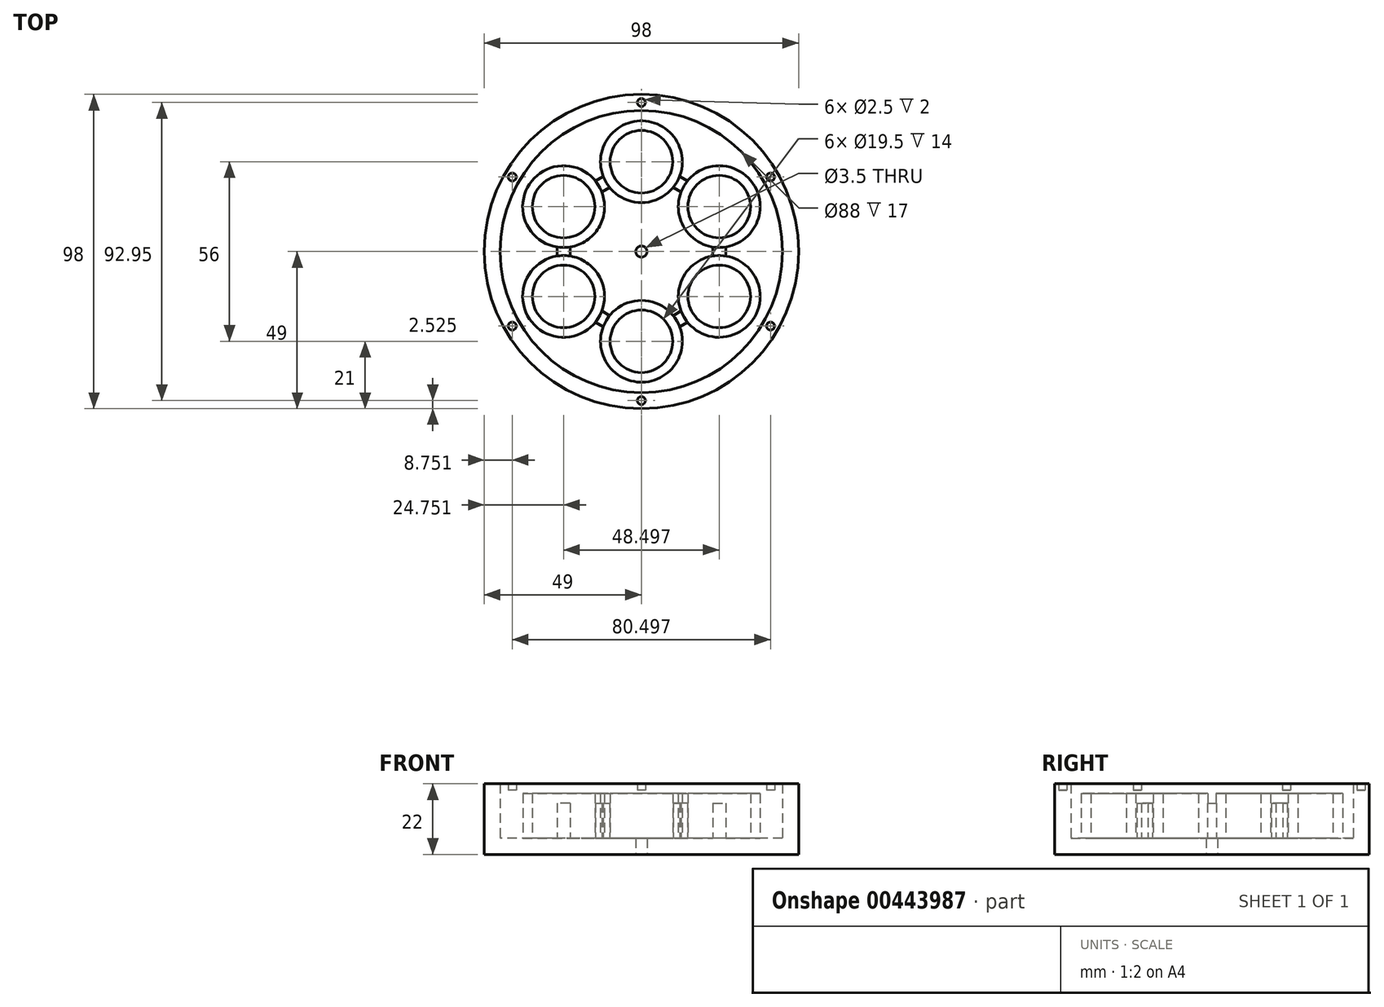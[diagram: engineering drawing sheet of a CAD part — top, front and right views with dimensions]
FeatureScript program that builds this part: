
annotation { "Feature Type Name" : "Feature", "Feature Type Description" : "" }
export const myFeature = defineFeature(function(context is Context, id is Id, definition is map)
    precondition{}
    {
        {
            var Q0;
            Q0=qCreatedBy(makeId("Top.planeOp"),FACE);
            var sketch = newSketch(context, id + "F0", { "sketchPlane" : qUnion([Q0])});
            skCircle(sketch, "E0", {"center": v(0, 0) * mm, "radius": 44 * mm});
            skLineSegment(sketch, "E1", {"start": v(0, -28) * mm, "end": v(-24.25, -14) * mm, "construction": true});
            skLineSegment(sketch, "E2", {"start": v(-24.25, -14) * mm, "end": v(-24.25, 14) * mm, "construction": true});
            skLineSegment(sketch, "E3", {"start": v(-24.25, 14) * mm, "end": v(0, 28) * mm, "construction": true});
            skLineSegment(sketch, "E4", {"start": v(0, 28) * mm, "end": v(24.25, 14) * mm, "construction": true});
            skLineSegment(sketch, "E5", {"start": v(24.25, 14) * mm, "end": v(24.25, -14) * mm, "construction": true});
            skLineSegment(sketch, "E6", {"start": v(24.25, -14) * mm, "end": v(0, -28) * mm, "construction": true});
            skLineSegment(sketch, "E7", {"start": v(24.25, 0) * mm, "end": v(17.35, 0) * mm, "construction": true});
            skPoint(sketch, "E7.endSnap0", {"position": v(24.25, 0) * mm});
            skCircle(sketch, "E8", {"center": v(0, 28) * mm, "radius": 9.75 * mm});
            skCircle(sketch, "E9", {"center": v(-24.25, 14) * mm, "radius": 9.75 * mm});
            skCircle(sketch, "E10", {"center": v(24.25, 14) * mm, "radius": 9.75 * mm});
            skCircle(sketch, "E11", {"center": v(24.25, -14) * mm, "radius": 9.75 * mm});
            skCircle(sketch, "E12", {"center": v(0, -28) * mm, "radius": 9.75 * mm});
            skCircle(sketch, "E13", {"center": v(-24.25, -14) * mm, "radius": 9.75 * mm});
            skCircle(sketch, "E14", {"center": v(0, 0) * mm, "radius": 1.75 * mm});
            skLineSegment(sketch, "E15", {"start": v(-24.25, 0) * mm, "end": v(-21.1, 0) * mm, "construction": true});
            skPoint(sketch, "E15.endSnap0", {"position": v(-24.25, 0) * mm});
            skCircle(sketch, "E16.0", {"center": v(-24.25, 14) * mm, "radius": 12.75 * mm});
            skCircle(sketch, "E17", {"center": v(-24.25, -14) * mm, "radius": 12.75 * mm});
            skCircle(sketch, "E18", {"center": v(0, -28) * mm, "radius": 12.75 * mm});
            skCircle(sketch, "E19", {"center": v(24.25, -14) * mm, "radius": 12.75 * mm});
            skCircle(sketch, "E20", {"center": v(24.25, 14) * mm, "radius": 12.75 * mm});
            skCircle(sketch, "E21", {"center": v(0, 28) * mm, "radius": 12.75 * mm});
            skCircle(sketch, "E22.0", {"center": v(0, 0) * mm, "radius": 49 * mm});
            skLineSegment(sketch, "E23.0", {"start": v(-22.25, -12.85) * mm, "end": v(-22.25, 12.85) * mm});
            skLineSegment(sketch, "E23.1", {"start": v(0, 25.7) * mm, "end": v(22.25, 12.85) * mm});
            skLineSegment(sketch, "E23.2", {"start": v(22.25, 12.85) * mm, "end": v(22.25, -12.85) * mm});
            skLineSegment(sketch, "E23.3", {"start": v(-22.25, 12.85) * mm, "end": v(0, 25.7) * mm});
            skLineSegment(sketch, "E23.4", {"start": v(22.25, -12.85) * mm, "end": v(0, -25.7) * mm});
            skLineSegment(sketch, "E23.5", {"start": v(0, -25.7) * mm, "end": v(-22.25, -12.85) * mm});
            skLineSegment(sketch, "E24.0", {"start": v(-26.25, -15.15) * mm, "end": v(-26.25, 15.15) * mm});
            skLineSegment(sketch, "E24.1", {"start": v(0, 30.3) * mm, "end": v(26.25, 15.15) * mm});
            skLineSegment(sketch, "E24.2", {"start": v(26.25, 15.15) * mm, "end": v(26.25, -15.15) * mm});
            skLineSegment(sketch, "E24.3", {"start": v(-26.25, 15.15) * mm, "end": v(0, 30.3) * mm});
            skLineSegment(sketch, "E24.4", {"start": v(26.25, -15.15) * mm, "end": v(0, -30.3) * mm});
            skLineSegment(sketch, "E24.5", {"start": v(0, -30.3) * mm, "end": v(-26.25, -15.15) * mm});
            skLineSegment(sketch, "E25.0", {"start": v(-40.25, -23.24) * mm, "end": v(-40.25, 23.24) * mm, "construction": true});
            skLineSegment(sketch, "E25.1", {"start": v(0, 46.48) * mm, "end": v(40.25, 23.24) * mm, "construction": true});
            skLineSegment(sketch, "E25.2", {"start": v(40.25, 23.24) * mm, "end": v(40.25, -23.24) * mm, "construction": true});
            skLineSegment(sketch, "E25.3", {"start": v(-40.25, 23.24) * mm, "end": v(0, 46.48) * mm, "construction": true});
            skLineSegment(sketch, "E25.4", {"start": v(40.25, -23.24) * mm, "end": v(0, -46.48) * mm, "construction": true});
            skLineSegment(sketch, "E25.5", {"start": v(0, -46.48) * mm, "end": v(-40.25, -23.24) * mm, "construction": true});
            skCircle(sketch, "E26", {"center": v(-40.25, 23.24) * mm, "radius": 1.25 * mm});
            skCircle(sketch, "E27", {"center": v(0, 46.48) * mm, "radius": 1.25 * mm});
            skCircle(sketch, "E28", {"center": v(40.25, 23.24) * mm, "radius": 1.25 * mm});
            skCircle(sketch, "E29", {"center": v(-40.25, -23.24) * mm, "radius": 1.25 * mm});
            skCircle(sketch, "E30", {"center": v(0, -46.48) * mm, "radius": 1.25 * mm});
            skCircle(sketch, "E31", {"center": v(40.25, -23.24) * mm, "radius": 1.25 * mm});
            skSolve(sketch);
        }
        {
            var Q0;
            {var subQ0=sQuery(id+"F0.wireOp",EDGE,"E24.5");var subQ1=sQuery(id+"F0.wireOp",EDGE,"E17");var subQ2=makeQuery(id+"F0.imprint","INTERSECT",VERTEX,{"derivedFrom":[subQ1,subQ0]});Q0=makeQuery(id+"F0.imprint","IMPRINT",FACE,{"disambiguationData":[TD([[makeQuery(id+"F0.imprint","IMPRINT",EDGE,{"disambiguationData":[TD([[subQ2,-1.0]])],"derivedFrom":subQ1}),-1.0]])]});}
            var Q1;
            {var subQ0=sQuery(id+"F0.wireOp",EDGE,"E23.5");var subQ1=sQuery(id+"F0.wireOp",EDGE,"E12");var subQ2=makeQuery(id+"F0.imprint","INTERSECT",VERTEX,{"derivedFrom":[subQ1,subQ0]});Q1=makeQuery(id+"F0.imprint","IMPRINT",FACE,{"disambiguationData":[TD([[makeQuery(id+"F0.imprint","IMPRINT",EDGE,{"disambiguationData":[TD([[subQ2,-1.0]])],"derivedFrom":subQ1}),-1.0]])]});}
            var Q2;
            {var subQ0=sQuery(id+"F0.wireOp",EDGE,"E24.1");var subQ1=sQuery(id+"F0.wireOp",EDGE,"E10");var subQ2=makeQuery(id+"F0.imprint","INTERSECT",VERTEX,{"derivedFrom":[subQ1,subQ0]});Q2=makeQuery(id+"F0.imprint","IMPRINT",FACE,{"disambiguationData":[TD([[makeQuery(id+"F0.imprint","IMPRINT",EDGE,{"disambiguationData":[TD([[subQ2,1.0]])],"derivedFrom":subQ1}),1.0]])]});}
            var Q3;
            Q3=makeQuery(id+"F0.imprint","IMPRINT",FACE,{"disambiguationData":[TD([[makeQuery(id+"F0.imprint","IMPRINT",EDGE,{"derivedFrom":sQuery(id+"F0.wireOp",EDGE,"E14")}),-1.0]])]});
            var Q4;
            {var subQ0=sQuery(id+"F0.wireOp",EDGE,"E24.2");var subQ1=sQuery(id+"F0.wireOp",EDGE,"E11");var subQ2=makeQuery(id+"F0.imprint","INTERSECT",VERTEX,{"derivedFrom":[subQ1,subQ0]});Q4=makeQuery(id+"F0.imprint","IMPRINT",FACE,{"disambiguationData":[TD([[makeQuery(id+"F0.imprint","IMPRINT",EDGE,{"disambiguationData":[TD([[subQ2,1.0]])],"derivedFrom":subQ1}),-1.0]])]});}
            var Q5;
            {var subQ0=sQuery(id+"F0.wireOp",EDGE,"E24.5");var subQ1=sQuery(id+"F0.wireOp",EDGE,"E13");var subQ2=makeQuery(id+"F0.imprint","INTERSECT",VERTEX,{"derivedFrom":[subQ1,subQ0]});Q5=makeQuery(id+"F0.imprint","IMPRINT",FACE,{"disambiguationData":[TD([[makeQuery(id+"F0.imprint","IMPRINT",EDGE,{"disambiguationData":[TD([[subQ2,-1.0]])],"derivedFrom":subQ1}),-1.0]])]});}
            var Q6;
            {var subQ0=sQuery(id+"F0.wireOp",EDGE,"E24.3");var subQ1=sQuery(id+"F0.wireOp",EDGE,"E8");var subQ2=makeQuery(id+"F0.imprint","INTERSECT",VERTEX,{"derivedFrom":[subQ1,subQ0]});Q6=makeQuery(id+"F0.imprint","IMPRINT",FACE,{"disambiguationData":[TD([[makeQuery(id+"F0.imprint","IMPRINT",EDGE,{"disambiguationData":[TD([[subQ2,1.0]])],"derivedFrom":subQ1}),-1.0]])]});}
            var Q7;
            {var subQ0=sQuery(id+"F0.wireOp",EDGE,"E24.3");var subQ1=sQuery(id+"F0.wireOp",EDGE,"E9");var subQ2=makeQuery(id+"F0.imprint","INTERSECT",VERTEX,{"derivedFrom":[subQ1,subQ0]});Q7=makeQuery(id+"F0.imprint","IMPRINT",FACE,{"disambiguationData":[TD([[makeQuery(id+"F0.imprint","IMPRINT",EDGE,{"disambiguationData":[TD([[subQ2,1.0]])],"derivedFrom":subQ1}),-1.0]])]});}
            var Q8;
            {var subQ0=sQuery(id+"F0.wireOp",EDGE,"E24.0");var subQ1=sQuery(id+"F0.wireOp",EDGE,"E9");var subQ2=makeQuery(id+"F0.imprint","INTERSECT",VERTEX,{"derivedFrom":[subQ1,subQ0]});Q8=makeQuery(id+"F0.imprint","IMPRINT",FACE,{"disambiguationData":[TD([[makeQuery(id+"F0.imprint","IMPRINT",EDGE,{"disambiguationData":[TD([[subQ2,-1.0]])],"derivedFrom":subQ1}),-1.0]])]});}
            var Q9;
            {var subQ0=sQuery(id+"F0.wireOp",EDGE,"E23.1");var subQ1=sQuery(id+"F0.wireOp",EDGE,"E8");var subQ2=makeQuery(id+"F0.imprint","INTERSECT",VERTEX,{"derivedFrom":[subQ1,subQ0]});Q9=makeQuery(id+"F0.imprint","IMPRINT",FACE,{"disambiguationData":[TD([[makeQuery(id+"F0.imprint","IMPRINT",EDGE,{"disambiguationData":[TD([[subQ2,-1.0]])],"derivedFrom":subQ1}),-1.0]])]});}
            var Q10;
            {var subQ0=sQuery(id+"F0.wireOp",EDGE,"E23.2");var subQ1=sQuery(id+"F0.wireOp",EDGE,"E11");var subQ2=makeQuery(id+"F0.imprint","INTERSECT",VERTEX,{"derivedFrom":[subQ1,subQ0]});Q10=makeQuery(id+"F0.imprint","IMPRINT",FACE,{"disambiguationData":[TD([[makeQuery(id+"F0.imprint","IMPRINT",EDGE,{"disambiguationData":[TD([[subQ2,-1.0]])],"derivedFrom":subQ1}),-1.0]])]});}
            var Q11;
            {var subQ0=sQuery(id+"F0.wireOp",EDGE,"E23.4");var subQ1=sQuery(id+"F0.wireOp",EDGE,"E12");var subQ2=makeQuery(id+"F0.imprint","INTERSECT",VERTEX,{"derivedFrom":[subQ1,subQ0]});Q11=makeQuery(id+"F0.imprint","IMPRINT",FACE,{"disambiguationData":[TD([[makeQuery(id+"F0.imprint","IMPRINT",EDGE,{"disambiguationData":[TD([[subQ2,1.0]])],"derivedFrom":subQ1}),-1.0]])]});}
            var Q12;
            {var subQ0=sQuery(id+"F0.wireOp",EDGE,"E23.0");var subQ1=sQuery(id+"F0.wireOp",EDGE,"E13");var subQ2=makeQuery(id+"F0.imprint","INTERSECT",VERTEX,{"derivedFrom":[subQ1,subQ0]});Q12=makeQuery(id+"F0.imprint","IMPRINT",FACE,{"disambiguationData":[TD([[makeQuery(id+"F0.imprint","IMPRINT",EDGE,{"disambiguationData":[TD([[subQ2,1.0]])],"derivedFrom":subQ1}),1.0]])]});}
            var Q13;
            {var subQ0=sQuery(id+"F0.wireOp",EDGE,"E24.4");var subQ1=sQuery(id+"F0.wireOp",EDGE,"E12");var subQ2=makeQuery(id+"F0.imprint","INTERSECT",VERTEX,{"derivedFrom":[subQ1,subQ0]});Q13=makeQuery(id+"F0.imprint","IMPRINT",FACE,{"disambiguationData":[TD([[makeQuery(id+"F0.imprint","IMPRINT",EDGE,{"disambiguationData":[TD([[subQ2,1.0]])],"derivedFrom":subQ1}),1.0]])]});}
            var Q14;
            {var subQ0=sQuery(id+"F0.wireOp",EDGE,"E23.1");var subQ1=sQuery(id+"F0.wireOp",EDGE,"E20");var subQ2=makeQuery(id+"F0.imprint","INTERSECT",VERTEX,{"derivedFrom":[subQ1,subQ0]});Q14=makeQuery(id+"F0.imprint","IMPRINT",FACE,{"disambiguationData":[TD([[makeQuery(id+"F0.imprint","IMPRINT",EDGE,{"disambiguationData":[TD([[subQ2,1.0]])],"derivedFrom":subQ1}),-1.0]])]});}
            var Q15;
            {var subQ0=sQuery(id+"F0.wireOp",EDGE,"E23.2");var subQ1=sQuery(id+"F0.wireOp",EDGE,"E10");var subQ2=makeQuery(id+"F0.imprint","INTERSECT",VERTEX,{"derivedFrom":[subQ1,subQ0]});Q15=makeQuery(id+"F0.imprint","IMPRINT",FACE,{"disambiguationData":[TD([[makeQuery(id+"F0.imprint","IMPRINT",EDGE,{"disambiguationData":[TD([[subQ2,-1.0]])],"derivedFrom":subQ1}),-1.0]])]});}
            var Q16;
            {var subQ0=sQuery(id+"F0.wireOp",EDGE,"E23.3");var subQ1=sQuery(id+"F0.wireOp",EDGE,"E8");var subQ2=makeQuery(id+"F0.imprint","INTERSECT",VERTEX,{"derivedFrom":[subQ1,subQ0]});Q16=makeQuery(id+"F0.imprint","IMPRINT",FACE,{"disambiguationData":[TD([[makeQuery(id+"F0.imprint","IMPRINT",EDGE,{"disambiguationData":[TD([[subQ2,1.0]])],"derivedFrom":subQ1}),-1.0]])]});}
            var Q17;
            {var subQ0=sQuery(id+"F0.wireOp",EDGE,"E24.4");var subQ1=sQuery(id+"F0.wireOp",EDGE,"E12");var subQ2=makeQuery(id+"F0.imprint","INTERSECT",VERTEX,{"derivedFrom":[subQ1,subQ0]});Q17=makeQuery(id+"F0.imprint","IMPRINT",FACE,{"disambiguationData":[TD([[makeQuery(id+"F0.imprint","IMPRINT",EDGE,{"disambiguationData":[TD([[subQ2,1.0]])],"derivedFrom":subQ1}),-1.0]])]});}
            var Q18;
            {var subQ0=sQuery(id+"F0.wireOp",EDGE,"E23.4");var subQ1=sQuery(id+"F0.wireOp",EDGE,"E12");var subQ2=makeQuery(id+"F0.imprint","INTERSECT",VERTEX,{"derivedFrom":[subQ1,subQ0]});Q18=makeQuery(id+"F0.imprint","IMPRINT",FACE,{"disambiguationData":[TD([[makeQuery(id+"F0.imprint","IMPRINT",EDGE,{"disambiguationData":[TD([[subQ2,-1.0]])],"derivedFrom":subQ1}),1.0]])]});}
            var Q19;
            {var subQ3=sQuery(id+"F0.wireOp",EDGE,"E13");var subQ8=sQuery(id+"F0.wireOp",EDGE,"E24.0");var subQ9=makeQuery(id+"F0.imprint","INTERSECT",VERTEX,{"derivedFrom":[subQ3,subQ8]});Q19=makeQuery(id+"F0.imprint","IMPRINT",FACE,{"disambiguationData":[TD([[makeQuery(id+"F0.imprint","IMPRINT",EDGE,{"disambiguationData":[TD([[subQ9,1.0]])],"derivedFrom":subQ3}),1.0]])]});}
            var Q20;
            {var subQ0=sQuery(id+"F0.wireOp",EDGE,"E24.2");var subQ1=sQuery(id+"F0.wireOp",EDGE,"E11");var subQ2=makeQuery(id+"F0.imprint","INTERSECT",VERTEX,{"derivedFrom":[subQ1,subQ0]});Q20=makeQuery(id+"F0.imprint","IMPRINT",FACE,{"disambiguationData":[TD([[makeQuery(id+"F0.imprint","IMPRINT",EDGE,{"disambiguationData":[TD([[subQ2,1.0]])],"derivedFrom":subQ1}),1.0]])]});}
            var Q21;
            {var subQ0=sQuery(id+"F0.wireOp",EDGE,"E24.3");var subQ1=sQuery(id+"F0.wireOp",EDGE,"E9");var subQ2=makeQuery(id+"F0.imprint","INTERSECT",VERTEX,{"derivedFrom":[subQ1,subQ0]});Q21=makeQuery(id+"F0.imprint","IMPRINT",FACE,{"disambiguationData":[TD([[makeQuery(id+"F0.imprint","IMPRINT",EDGE,{"disambiguationData":[TD([[subQ2,-1.0]])],"derivedFrom":subQ1}),-1.0]])]});}
            var Q22;
            {var subQ0=sQuery(id+"F0.wireOp",EDGE,"E23.4");var subQ1=sQuery(id+"F0.wireOp",EDGE,"E18");var subQ2=makeQuery(id+"F0.imprint","INTERSECT",VERTEX,{"derivedFrom":[subQ1,subQ0]});Q22=makeQuery(id+"F0.imprint","IMPRINT",FACE,{"disambiguationData":[TD([[makeQuery(id+"F0.imprint","IMPRINT",EDGE,{"disambiguationData":[TD([[subQ2,1.0]])],"derivedFrom":subQ1}),-1.0]])]});}
            var Q23;
            {var subQ0=sQuery(id+"F0.wireOp",EDGE,"E23.3");var subQ1=sQuery(id+"F0.wireOp",EDGE,"E9");var subQ2=makeQuery(id+"F0.imprint","INTERSECT",VERTEX,{"derivedFrom":[subQ1,subQ0]});Q23=makeQuery(id+"F0.imprint","IMPRINT",FACE,{"disambiguationData":[TD([[makeQuery(id+"F0.imprint","IMPRINT",EDGE,{"disambiguationData":[TD([[subQ2,1.0]])],"derivedFrom":subQ1}),1.0]])]});}
            var Q24;
            {var subQ0=sQuery(id+"F0.wireOp",EDGE,"E24.0");var subQ1=sQuery(id+"F0.wireOp",EDGE,"E13");var subQ2=makeQuery(id+"F0.imprint","INTERSECT",VERTEX,{"derivedFrom":[subQ1,subQ0]});Q24=makeQuery(id+"F0.imprint","IMPRINT",FACE,{"disambiguationData":[TD([[makeQuery(id+"F0.imprint","IMPRINT",EDGE,{"disambiguationData":[TD([[subQ2,-1.0]])],"derivedFrom":subQ1}),1.0]])]});}
            var Q25;
            {var subQ0=sQuery(id+"F0.wireOp",EDGE,"E23.1");var subQ1=sQuery(id+"F0.wireOp",EDGE,"E10");var subQ2=makeQuery(id+"F0.imprint","INTERSECT",VERTEX,{"derivedFrom":[subQ1,subQ0]});Q25=makeQuery(id+"F0.imprint","IMPRINT",FACE,{"disambiguationData":[TD([[makeQuery(id+"F0.imprint","IMPRINT",EDGE,{"disambiguationData":[TD([[subQ2,-1.0]])],"derivedFrom":subQ1}),1.0]])]});}
            var Q26;
            {var subQ0=sQuery(id+"F0.wireOp",EDGE,"E24.3");var subQ1=sQuery(id+"F0.wireOp",EDGE,"E8");var subQ2=makeQuery(id+"F0.imprint","INTERSECT",VERTEX,{"derivedFrom":[subQ1,subQ0]});Q26=makeQuery(id+"F0.imprint","IMPRINT",FACE,{"disambiguationData":[TD([[makeQuery(id+"F0.imprint","IMPRINT",EDGE,{"disambiguationData":[TD([[subQ2,1.0]])],"derivedFrom":subQ1}),1.0]])]});}
            var Q27;
            {var subQ0=sQuery(id+"F0.wireOp",EDGE,"E24.3");var subQ1=sQuery(id+"F0.wireOp",EDGE,"E16.0");var subQ2=makeQuery(id+"F0.imprint","INTERSECT",VERTEX,{"derivedFrom":[subQ1,subQ0]});Q27=makeQuery(id+"F0.imprint","IMPRINT",FACE,{"disambiguationData":[TD([[makeQuery(id+"F0.imprint","IMPRINT",EDGE,{"disambiguationData":[TD([[subQ2,1.0]])],"derivedFrom":subQ1}),-1.0]])]});}
            var Q28;
            {var subQ0=sQuery(id+"F0.wireOp",EDGE,"E23.4");var subQ1=sQuery(id+"F0.wireOp",EDGE,"E12");var subQ2=makeQuery(id+"F0.imprint","INTERSECT",VERTEX,{"derivedFrom":[subQ1,subQ0]});Q28=makeQuery(id+"F0.imprint","IMPRINT",FACE,{"disambiguationData":[TD([[makeQuery(id+"F0.imprint","IMPRINT",EDGE,{"disambiguationData":[TD([[subQ2,-1.0]])],"derivedFrom":subQ1}),-1.0]])]});}
            var Q29;
            {var subQ0=sQuery(id+"F0.wireOp",EDGE,"E23.3");var subQ1=sQuery(id+"F0.wireOp",EDGE,"E8");var subQ2=makeQuery(id+"F0.imprint","INTERSECT",VERTEX,{"derivedFrom":[subQ1,subQ0]});Q29=makeQuery(id+"F0.imprint","IMPRINT",FACE,{"disambiguationData":[TD([[makeQuery(id+"F0.imprint","IMPRINT",EDGE,{"disambiguationData":[TD([[subQ2,-1.0]])],"derivedFrom":subQ1}),-1.0]])]});}
            var Q30;
            {var subQ0=sQuery(id+"F0.wireOp",EDGE,"E24.0");var subQ1=sQuery(id+"F0.wireOp",EDGE,"E13");var subQ2=makeQuery(id+"F0.imprint","INTERSECT",VERTEX,{"derivedFrom":[subQ1,subQ0]});Q30=makeQuery(id+"F0.imprint","IMPRINT",FACE,{"disambiguationData":[TD([[makeQuery(id+"F0.imprint","IMPRINT",EDGE,{"disambiguationData":[TD([[subQ2,-1.0]])],"derivedFrom":subQ1}),-1.0]])]});}
            var Q31;
            {var subQ0=sQuery(id+"F0.wireOp",EDGE,"E23.1");var subQ1=sQuery(id+"F0.wireOp",EDGE,"E10");var subQ2=makeQuery(id+"F0.imprint","INTERSECT",VERTEX,{"derivedFrom":[subQ1,subQ0]});Q31=makeQuery(id+"F0.imprint","IMPRINT",FACE,{"disambiguationData":[TD([[makeQuery(id+"F0.imprint","IMPRINT",EDGE,{"disambiguationData":[TD([[subQ2,1.0]])],"derivedFrom":subQ1}),-1.0]])]});}
            var Q32;
            {var subQ0=sQuery(id+"F0.wireOp",EDGE,"E24.1");var subQ1=sQuery(id+"F0.wireOp",EDGE,"E10");var subQ2=makeQuery(id+"F0.imprint","INTERSECT",VERTEX,{"derivedFrom":[subQ1,subQ0]});Q32=makeQuery(id+"F0.imprint","IMPRINT",FACE,{"disambiguationData":[TD([[makeQuery(id+"F0.imprint","IMPRINT",EDGE,{"disambiguationData":[TD([[subQ2,1.0]])],"derivedFrom":subQ1}),-1.0]])]});}
            var Q33;
            {var subQ0=sQuery(id+"F0.wireOp",EDGE,"E23.3");var subQ1=sQuery(id+"F0.wireOp",EDGE,"E9");var subQ2=makeQuery(id+"F0.imprint","INTERSECT",VERTEX,{"derivedFrom":[subQ1,subQ0]});Q33=makeQuery(id+"F0.imprint","IMPRINT",FACE,{"disambiguationData":[TD([[makeQuery(id+"F0.imprint","IMPRINT",EDGE,{"disambiguationData":[TD([[subQ2,1.0]])],"derivedFrom":subQ1}),-1.0]])]});}
            var Q34;
            {var subQ1=sQuery(id+"F0.wireOp",EDGE,"E23.4");var subQ3=sQuery(id+"F0.wireOp",EDGE,"E12");var subQ5=makeQuery(id+"F0.imprint","INTERSECT",VERTEX,{"derivedFrom":[subQ3,subQ1]});Q34=makeQuery(id+"F0.imprint","IMPRINT",FACE,{"disambiguationData":[TD([[makeQuery(id+"F0.imprint","IMPRINT",EDGE,{"disambiguationData":[TD([[subQ5,1.0]])],"derivedFrom":subQ3}),1.0]])]});}
            var Q35;
            {var subQ0=sQuery(id+"F0.wireOp",EDGE,"E24.3");var subQ1=sQuery(id+"F0.wireOp",EDGE,"E9");var subQ2=makeQuery(id+"F0.imprint","INTERSECT",VERTEX,{"derivedFrom":[subQ1,subQ0]});Q35=makeQuery(id+"F0.imprint","IMPRINT",FACE,{"disambiguationData":[TD([[makeQuery(id+"F0.imprint","IMPRINT",EDGE,{"disambiguationData":[TD([[subQ2,-1.0]])],"derivedFrom":subQ1}),1.0]])]});}
            var Q36;
            {var subQ0=sQuery(id+"F0.wireOp",EDGE,"E23.0");var subQ1=sQuery(id+"F0.wireOp",EDGE,"E13");var subQ2=makeQuery(id+"F0.imprint","INTERSECT",VERTEX,{"derivedFrom":[subQ1,subQ0]});Q36=makeQuery(id+"F0.imprint","IMPRINT",FACE,{"disambiguationData":[TD([[makeQuery(id+"F0.imprint","IMPRINT",EDGE,{"disambiguationData":[TD([[subQ2,1.0]])],"derivedFrom":subQ1}),-1.0]])]});}
            var Q37;
            {var subQ0=sQuery(id+"F0.wireOp",EDGE,"E24.0");var subQ1=sQuery(id+"F0.wireOp",EDGE,"E13");var subQ2=makeQuery(id+"F0.imprint","INTERSECT",VERTEX,{"derivedFrom":[subQ1,subQ0]});Q37=makeQuery(id+"F0.imprint","IMPRINT",FACE,{"disambiguationData":[TD([[makeQuery(id+"F0.imprint","IMPRINT",EDGE,{"disambiguationData":[TD([[subQ2,1.0]])],"derivedFrom":subQ1}),-1.0]])]});}
            var Q38;
            {var subQ0=sQuery(id+"F0.wireOp",EDGE,"E23.2");var subQ1=sQuery(id+"F0.wireOp",EDGE,"E11");var subQ2=makeQuery(id+"F0.imprint","INTERSECT",VERTEX,{"derivedFrom":[subQ1,subQ0]});Q38=makeQuery(id+"F0.imprint","IMPRINT",FACE,{"disambiguationData":[TD([[makeQuery(id+"F0.imprint","IMPRINT",EDGE,{"disambiguationData":[TD([[subQ2,-1.0]])],"derivedFrom":subQ1}),1.0]])]});}
            var Q39;
            Q39=makeQuery(id+"F0.imprint","IMPRINT",FACE,{"disambiguationData":[TD([[makeQuery(id+"F0.imprint","IMPRINT",EDGE,{"derivedFrom":sQuery(id+"F0.wireOp",EDGE,"E0")}),1.0]])]});
            var Q40;
            {var subQ0=sQuery(id+"F0.wireOp",EDGE,"E23.2");var subQ1=sQuery(id+"F0.wireOp",EDGE,"E11");var subQ2=makeQuery(id+"F0.imprint","INTERSECT",VERTEX,{"derivedFrom":[subQ1,subQ0]});Q40=makeQuery(id+"F0.imprint","IMPRINT",FACE,{"disambiguationData":[TD([[makeQuery(id+"F0.imprint","IMPRINT",EDGE,{"disambiguationData":[TD([[subQ2,1.0]])],"derivedFrom":subQ1}),-1.0]])]});}
            var Q41;
            {var subQ1=sQuery(id+"F0.wireOp",EDGE,"E23.1");var subQ3=sQuery(id+"F0.wireOp",EDGE,"E10");var subQ4=makeQuery(id+"F0.imprint","INTERSECT",VERTEX,{"derivedFrom":[subQ3,subQ1]});Q41=makeQuery(id+"F0.imprint","IMPRINT",FACE,{"disambiguationData":[TD([[makeQuery(id+"F0.imprint","IMPRINT",EDGE,{"disambiguationData":[TD([[subQ4,1.0]])],"derivedFrom":subQ3}),1.0]])]});}
            var Q42;
            {var subQ0=sQuery(id+"F0.wireOp",EDGE,"E23.3");var subQ1=sQuery(id+"F0.wireOp",EDGE,"E8");var subQ2=makeQuery(id+"F0.imprint","INTERSECT",VERTEX,{"derivedFrom":[subQ1,subQ0]});Q42=makeQuery(id+"F0.imprint","IMPRINT",FACE,{"disambiguationData":[TD([[makeQuery(id+"F0.imprint","IMPRINT",EDGE,{"disambiguationData":[TD([[subQ2,-1.0]])],"derivedFrom":subQ1}),1.0]])]});}
            var Q43;
            {var subQ0=sQuery(id+"F0.wireOp",EDGE,"E23.4");var subQ1=sQuery(id+"F0.wireOp",EDGE,"E11");var subQ2=makeQuery(id+"F0.imprint","INTERSECT",VERTEX,{"derivedFrom":[subQ1,subQ0]});Q43=makeQuery(id+"F0.imprint","IMPRINT",FACE,{"disambiguationData":[TD([[makeQuery(id+"F0.imprint","IMPRINT",EDGE,{"disambiguationData":[TD([[subQ2,-1.0]])],"derivedFrom":subQ1}),-1.0]])]});}
            var Q44;
            {var subQ0=sQuery(id+"F0.wireOp",EDGE,"E23.2");var subQ1=sQuery(id+"F0.wireOp",EDGE,"E19");var subQ2=makeQuery(id+"F0.imprint","INTERSECT",VERTEX,{"derivedFrom":[subQ1,subQ0]});Q44=makeQuery(id+"F0.imprint","IMPRINT",FACE,{"disambiguationData":[TD([[makeQuery(id+"F0.imprint","IMPRINT",EDGE,{"disambiguationData":[TD([[subQ2,1.0]])],"derivedFrom":subQ1}),-1.0]])]});}
            var Q45;
            {var subQ0=sQuery(id+"F0.wireOp",EDGE,"E23.3");var subQ3=sQuery(id+"F0.wireOp",EDGE,"E8");var subQ4=makeQuery(id+"F0.imprint","INTERSECT",VERTEX,{"derivedFrom":[subQ3,subQ0]});Q45=makeQuery(id+"F0.imprint","IMPRINT",FACE,{"disambiguationData":[TD([[makeQuery(id+"F0.imprint","IMPRINT",EDGE,{"disambiguationData":[TD([[subQ4,1.0]])],"derivedFrom":subQ3}),1.0]])]});}
            var Q46;
            {var subQ1=sQuery(id+"F0.wireOp",EDGE,"E23.2");var subQ3=sQuery(id+"F0.wireOp",EDGE,"E11");var subQ5=makeQuery(id+"F0.imprint","INTERSECT",VERTEX,{"derivedFrom":[subQ3,subQ1]});Q46=makeQuery(id+"F0.imprint","IMPRINT",FACE,{"disambiguationData":[TD([[makeQuery(id+"F0.imprint","IMPRINT",EDGE,{"disambiguationData":[TD([[subQ5,1.0]])],"derivedFrom":subQ3}),1.0]])]});}
            var Q47;
            {var subQ0=sQuery(id+"F0.wireOp",EDGE,"E24.0");var subQ1=sQuery(id+"F0.wireOp",EDGE,"E16.0");var subQ2=makeQuery(id+"F0.imprint","INTERSECT",VERTEX,{"derivedFrom":[subQ1,subQ0]});Q47=makeQuery(id+"F0.imprint","IMPRINT",FACE,{"disambiguationData":[TD([[makeQuery(id+"F0.imprint","IMPRINT",EDGE,{"disambiguationData":[TD([[subQ2,-1.0]])],"derivedFrom":subQ1}),-1.0]])]});}
            var Q48;
            {var subQ0=sQuery(id+"F0.wireOp",EDGE,"E23.1");var subQ1=sQuery(id+"F0.wireOp",EDGE,"E10");var subQ2=makeQuery(id+"F0.imprint","INTERSECT",VERTEX,{"derivedFrom":[subQ1,subQ0]});Q48=makeQuery(id+"F0.imprint","IMPRINT",FACE,{"disambiguationData":[TD([[makeQuery(id+"F0.imprint","IMPRINT",EDGE,{"disambiguationData":[TD([[subQ2,-1.0]])],"derivedFrom":subQ1}),-1.0]])]});}
            var Q49;
            {var subQ3=sQuery(id+"F0.wireOp",EDGE,"E9");var subQ8=sQuery(id+"F0.wireOp",EDGE,"E24.3");var subQ9=makeQuery(id+"F0.imprint","INTERSECT",VERTEX,{"derivedFrom":[subQ3,subQ8]});Q49=makeQuery(id+"F0.imprint","IMPRINT",FACE,{"disambiguationData":[TD([[makeQuery(id+"F0.imprint","IMPRINT",EDGE,{"disambiguationData":[TD([[subQ9,1.0]])],"derivedFrom":subQ3}),1.0]])]});}
            var Q50;
            Q50=makeQuery(id+"F0.imprint","IMPRINT",FACE,{"disambiguationData":[TD([[makeQuery(id+"F0.imprint","IMPRINT",EDGE,{"derivedFrom":sQuery(id+"F0.wireOp",EDGE,"E0")}),-1.0]])]});
            extrude(context, id + "F1", {"entities" : qUnion([Q0, Q1, Q2, Q3, Q4, Q5, Q6, Q7, Q8, Q9, Q10, Q11, Q12, Q13, Q14, Q15, Q16, Q17, Q18, Q19, Q20, Q21, Q22, Q23, Q24, Q25, Q26, Q27, Q28, Q29, Q30, Q31, Q32, Q33, Q34, Q35, Q36, Q37, Q38, Q39, Q40, Q41, Q42, Q43, Q44, Q45, Q46, Q47, Q48, Q49, Q50]), "depth" : 5 * mm});
        }
        {
            var Q0;
            Q0=makeQuery(id+"F0.imprint","IMPRINT",FACE,{"disambiguationData":[TD([[makeQuery(id+"F0.imprint","IMPRINT",EDGE,{"derivedFrom":sQuery(id+"F0.wireOp",EDGE,"E0")}),-1.0]])]});
            var Q1;
            {var subQ0=sQuery(id+"F0.wireOp",EDGE,"E23.3");var subQ1=sQuery(id+"F0.wireOp",EDGE,"E9");var subQ2=makeQuery(id+"F0.imprint","INTERSECT",VERTEX,{"derivedFrom":[subQ1,subQ0]});Q1=makeQuery(id+"F0.imprint","IMPRINT",FACE,{"disambiguationData":[TD([[makeQuery(id+"F0.imprint","IMPRINT",EDGE,{"disambiguationData":[TD([[subQ2,1.0]])],"derivedFrom":subQ1}),-1.0]])]});}
            var Q2;
            {var subQ0=sQuery(id+"F0.wireOp",EDGE,"E24.3");var subQ1=sQuery(id+"F0.wireOp",EDGE,"E9");var subQ2=makeQuery(id+"F0.imprint","INTERSECT",VERTEX,{"derivedFrom":[subQ1,subQ0]});Q2=makeQuery(id+"F0.imprint","IMPRINT",FACE,{"disambiguationData":[TD([[makeQuery(id+"F0.imprint","IMPRINT",EDGE,{"disambiguationData":[TD([[subQ2,1.0]])],"derivedFrom":subQ1}),-1.0]])]});}
            var Q3;
            {var subQ0=sQuery(id+"F0.wireOp",EDGE,"E24.3");var subQ1=sQuery(id+"F0.wireOp",EDGE,"E9");var subQ2=makeQuery(id+"F0.imprint","INTERSECT",VERTEX,{"derivedFrom":[subQ1,subQ0]});Q3=makeQuery(id+"F0.imprint","IMPRINT",FACE,{"disambiguationData":[TD([[makeQuery(id+"F0.imprint","IMPRINT",EDGE,{"disambiguationData":[TD([[subQ2,-1.0]])],"derivedFrom":subQ1}),-1.0]])]});}
            var Q4;
            {var subQ0=sQuery(id+"F0.wireOp",EDGE,"E24.0");var subQ1=sQuery(id+"F0.wireOp",EDGE,"E9");var subQ2=makeQuery(id+"F0.imprint","INTERSECT",VERTEX,{"derivedFrom":[subQ1,subQ0]});Q4=makeQuery(id+"F0.imprint","IMPRINT",FACE,{"disambiguationData":[TD([[makeQuery(id+"F0.imprint","IMPRINT",EDGE,{"disambiguationData":[TD([[subQ2,-1.0]])],"derivedFrom":subQ1}),-1.0]])]});}
            var Q5;
            {var subQ0=sQuery(id+"F0.wireOp",EDGE,"E23.3");var subQ1=sQuery(id+"F0.wireOp",EDGE,"E8");var subQ2=makeQuery(id+"F0.imprint","INTERSECT",VERTEX,{"derivedFrom":[subQ1,subQ0]});Q5=makeQuery(id+"F0.imprint","IMPRINT",FACE,{"disambiguationData":[TD([[makeQuery(id+"F0.imprint","IMPRINT",EDGE,{"disambiguationData":[TD([[subQ2,1.0]])],"derivedFrom":subQ1}),-1.0]])]});}
            var Q6;
            {var subQ0=sQuery(id+"F0.wireOp",EDGE,"E24.3");var subQ1=sQuery(id+"F0.wireOp",EDGE,"E8");var subQ2=makeQuery(id+"F0.imprint","INTERSECT",VERTEX,{"derivedFrom":[subQ1,subQ0]});Q6=makeQuery(id+"F0.imprint","IMPRINT",FACE,{"disambiguationData":[TD([[makeQuery(id+"F0.imprint","IMPRINT",EDGE,{"disambiguationData":[TD([[subQ2,1.0]])],"derivedFrom":subQ1}),-1.0]])]});}
            var Q7;
            {var subQ0=sQuery(id+"F0.wireOp",EDGE,"E23.1");var subQ1=sQuery(id+"F0.wireOp",EDGE,"E8");var subQ2=makeQuery(id+"F0.imprint","INTERSECT",VERTEX,{"derivedFrom":[subQ1,subQ0]});Q7=makeQuery(id+"F0.imprint","IMPRINT",FACE,{"disambiguationData":[TD([[makeQuery(id+"F0.imprint","IMPRINT",EDGE,{"disambiguationData":[TD([[subQ2,-1.0]])],"derivedFrom":subQ1}),-1.0]])]});}
            var Q8;
            {var subQ0=sQuery(id+"F0.wireOp",EDGE,"E23.3");var subQ1=sQuery(id+"F0.wireOp",EDGE,"E8");var subQ2=makeQuery(id+"F0.imprint","INTERSECT",VERTEX,{"derivedFrom":[subQ1,subQ0]});Q8=makeQuery(id+"F0.imprint","IMPRINT",FACE,{"disambiguationData":[TD([[makeQuery(id+"F0.imprint","IMPRINT",EDGE,{"disambiguationData":[TD([[subQ2,-1.0]])],"derivedFrom":subQ1}),-1.0]])]});}
            var Q9;
            {var subQ0=sQuery(id+"F0.wireOp",EDGE,"E23.1");var subQ1=sQuery(id+"F0.wireOp",EDGE,"E10");var subQ2=makeQuery(id+"F0.imprint","INTERSECT",VERTEX,{"derivedFrom":[subQ1,subQ0]});Q9=makeQuery(id+"F0.imprint","IMPRINT",FACE,{"disambiguationData":[TD([[makeQuery(id+"F0.imprint","IMPRINT",EDGE,{"disambiguationData":[TD([[subQ2,1.0]])],"derivedFrom":subQ1}),-1.0]])]});}
            var Q10;
            {var subQ0=sQuery(id+"F0.wireOp",EDGE,"E24.1");var subQ1=sQuery(id+"F0.wireOp",EDGE,"E10");var subQ2=makeQuery(id+"F0.imprint","INTERSECT",VERTEX,{"derivedFrom":[subQ1,subQ0]});Q10=makeQuery(id+"F0.imprint","IMPRINT",FACE,{"disambiguationData":[TD([[makeQuery(id+"F0.imprint","IMPRINT",EDGE,{"disambiguationData":[TD([[subQ2,1.0]])],"derivedFrom":subQ1}),-1.0]])]});}
            var Q11;
            {var subQ0=sQuery(id+"F0.wireOp",EDGE,"E23.1");var subQ1=sQuery(id+"F0.wireOp",EDGE,"E10");var subQ2=makeQuery(id+"F0.imprint","INTERSECT",VERTEX,{"derivedFrom":[subQ1,subQ0]});Q11=makeQuery(id+"F0.imprint","IMPRINT",FACE,{"disambiguationData":[TD([[makeQuery(id+"F0.imprint","IMPRINT",EDGE,{"disambiguationData":[TD([[subQ2,-1.0]])],"derivedFrom":subQ1}),-1.0]])]});}
            var Q12;
            {var subQ0=sQuery(id+"F0.wireOp",EDGE,"E23.2");var subQ1=sQuery(id+"F0.wireOp",EDGE,"E10");var subQ2=makeQuery(id+"F0.imprint","INTERSECT",VERTEX,{"derivedFrom":[subQ1,subQ0]});Q12=makeQuery(id+"F0.imprint","IMPRINT",FACE,{"disambiguationData":[TD([[makeQuery(id+"F0.imprint","IMPRINT",EDGE,{"disambiguationData":[TD([[subQ2,-1.0]])],"derivedFrom":subQ1}),-1.0]])]});}
            var Q13;
            {var subQ0=sQuery(id+"F0.wireOp",EDGE,"E24.0");var subQ1=sQuery(id+"F0.wireOp",EDGE,"E13");var subQ2=makeQuery(id+"F0.imprint","INTERSECT",VERTEX,{"derivedFrom":[subQ1,subQ0]});Q13=makeQuery(id+"F0.imprint","IMPRINT",FACE,{"disambiguationData":[TD([[makeQuery(id+"F0.imprint","IMPRINT",EDGE,{"disambiguationData":[TD([[subQ2,-1.0]])],"derivedFrom":subQ1}),-1.0]])]});}
            var Q14;
            {var subQ0=sQuery(id+"F0.wireOp",EDGE,"E24.0");var subQ1=sQuery(id+"F0.wireOp",EDGE,"E13");var subQ2=makeQuery(id+"F0.imprint","INTERSECT",VERTEX,{"derivedFrom":[subQ1,subQ0]});Q14=makeQuery(id+"F0.imprint","IMPRINT",FACE,{"disambiguationData":[TD([[makeQuery(id+"F0.imprint","IMPRINT",EDGE,{"disambiguationData":[TD([[subQ2,1.0]])],"derivedFrom":subQ1}),-1.0]])]});}
            var Q15;
            {var subQ0=sQuery(id+"F0.wireOp",EDGE,"E23.0");var subQ1=sQuery(id+"F0.wireOp",EDGE,"E13");var subQ2=makeQuery(id+"F0.imprint","INTERSECT",VERTEX,{"derivedFrom":[subQ1,subQ0]});Q15=makeQuery(id+"F0.imprint","IMPRINT",FACE,{"disambiguationData":[TD([[makeQuery(id+"F0.imprint","IMPRINT",EDGE,{"disambiguationData":[TD([[subQ2,1.0]])],"derivedFrom":subQ1}),-1.0]])]});}
            var Q16;
            {var subQ0=sQuery(id+"F0.wireOp",EDGE,"E24.5");var subQ1=sQuery(id+"F0.wireOp",EDGE,"E13");var subQ2=makeQuery(id+"F0.imprint","INTERSECT",VERTEX,{"derivedFrom":[subQ1,subQ0]});Q16=makeQuery(id+"F0.imprint","IMPRINT",FACE,{"disambiguationData":[TD([[makeQuery(id+"F0.imprint","IMPRINT",EDGE,{"disambiguationData":[TD([[subQ2,-1.0]])],"derivedFrom":subQ1}),-1.0]])]});}
            var Q17;
            {var subQ0=sQuery(id+"F0.wireOp",EDGE,"E23.5");var subQ1=sQuery(id+"F0.wireOp",EDGE,"E12");var subQ2=makeQuery(id+"F0.imprint","INTERSECT",VERTEX,{"derivedFrom":[subQ1,subQ0]});Q17=makeQuery(id+"F0.imprint","IMPRINT",FACE,{"disambiguationData":[TD([[makeQuery(id+"F0.imprint","IMPRINT",EDGE,{"disambiguationData":[TD([[subQ2,-1.0]])],"derivedFrom":subQ1}),-1.0]])]});}
            var Q18;
            {var subQ0=sQuery(id+"F0.wireOp",EDGE,"E23.4");var subQ1=sQuery(id+"F0.wireOp",EDGE,"E12");var subQ2=makeQuery(id+"F0.imprint","INTERSECT",VERTEX,{"derivedFrom":[subQ1,subQ0]});Q18=makeQuery(id+"F0.imprint","IMPRINT",FACE,{"disambiguationData":[TD([[makeQuery(id+"F0.imprint","IMPRINT",EDGE,{"disambiguationData":[TD([[subQ2,-1.0]])],"derivedFrom":subQ1}),-1.0]])]});}
            var Q19;
            {var subQ0=sQuery(id+"F0.wireOp",EDGE,"E24.4");var subQ1=sQuery(id+"F0.wireOp",EDGE,"E12");var subQ2=makeQuery(id+"F0.imprint","INTERSECT",VERTEX,{"derivedFrom":[subQ1,subQ0]});Q19=makeQuery(id+"F0.imprint","IMPRINT",FACE,{"disambiguationData":[TD([[makeQuery(id+"F0.imprint","IMPRINT",EDGE,{"disambiguationData":[TD([[subQ2,1.0]])],"derivedFrom":subQ1}),-1.0]])]});}
            var Q20;
            {var subQ0=sQuery(id+"F0.wireOp",EDGE,"E23.4");var subQ1=sQuery(id+"F0.wireOp",EDGE,"E12");var subQ2=makeQuery(id+"F0.imprint","INTERSECT",VERTEX,{"derivedFrom":[subQ1,subQ0]});Q20=makeQuery(id+"F0.imprint","IMPRINT",FACE,{"disambiguationData":[TD([[makeQuery(id+"F0.imprint","IMPRINT",EDGE,{"disambiguationData":[TD([[subQ2,1.0]])],"derivedFrom":subQ1}),-1.0]])]});}
            var Q21;
            {var subQ0=sQuery(id+"F0.wireOp",EDGE,"E23.4");var subQ1=sQuery(id+"F0.wireOp",EDGE,"E11");var subQ2=makeQuery(id+"F0.imprint","INTERSECT",VERTEX,{"derivedFrom":[subQ1,subQ0]});Q21=makeQuery(id+"F0.imprint","IMPRINT",FACE,{"disambiguationData":[TD([[makeQuery(id+"F0.imprint","IMPRINT",EDGE,{"disambiguationData":[TD([[subQ2,-1.0]])],"derivedFrom":subQ1}),-1.0]])]});}
            var Q22;
            {var subQ0=sQuery(id+"F0.wireOp",EDGE,"E23.2");var subQ1=sQuery(id+"F0.wireOp",EDGE,"E11");var subQ2=makeQuery(id+"F0.imprint","INTERSECT",VERTEX,{"derivedFrom":[subQ1,subQ0]});Q22=makeQuery(id+"F0.imprint","IMPRINT",FACE,{"disambiguationData":[TD([[makeQuery(id+"F0.imprint","IMPRINT",EDGE,{"disambiguationData":[TD([[subQ2,-1.0]])],"derivedFrom":subQ1}),-1.0]])]});}
            var Q23;
            {var subQ0=sQuery(id+"F0.wireOp",EDGE,"E24.2");var subQ1=sQuery(id+"F0.wireOp",EDGE,"E11");var subQ2=makeQuery(id+"F0.imprint","INTERSECT",VERTEX,{"derivedFrom":[subQ1,subQ0]});Q23=makeQuery(id+"F0.imprint","IMPRINT",FACE,{"disambiguationData":[TD([[makeQuery(id+"F0.imprint","IMPRINT",EDGE,{"disambiguationData":[TD([[subQ2,1.0]])],"derivedFrom":subQ1}),-1.0]])]});}
            var Q24;
            {var subQ0=sQuery(id+"F0.wireOp",EDGE,"E23.2");var subQ1=sQuery(id+"F0.wireOp",EDGE,"E11");var subQ2=makeQuery(id+"F0.imprint","INTERSECT",VERTEX,{"derivedFrom":[subQ1,subQ0]});Q24=makeQuery(id+"F0.imprint","IMPRINT",FACE,{"disambiguationData":[TD([[makeQuery(id+"F0.imprint","IMPRINT",EDGE,{"disambiguationData":[TD([[subQ2,1.0]])],"derivedFrom":subQ1}),-1.0]])]});}
            extrude(context, id + "F2", {"entities" : qUnion([Q0, Q1, Q2, Q3, Q4, Q5, Q6, Q7, Q8, Q9, Q10, Q11, Q12, Q13, Q14, Q15, Q16, Q17, Q18, Q19, Q20, Q21, Q22, Q23, Q24]), "operationType" : NewBodyOperationType.ADD, "depth" : 19 * mm});
        }
        {
            var Q0;
            {var subQ0=sQuery(id+"F0.wireOp",EDGE,"E24.3");var subQ1=sQuery(id+"F0.wireOp",EDGE,"E16.0");var subQ2=makeQuery(id+"F0.imprint","INTERSECT",VERTEX,{"derivedFrom":[subQ1,subQ0]});Q0=makeQuery(id+"F0.imprint","IMPRINT",FACE,{"disambiguationData":[TD([[makeQuery(id+"F0.imprint","IMPRINT",EDGE,{"disambiguationData":[TD([[subQ2,1.0]])],"derivedFrom":subQ1}),-1.0]])]});}
            var Q1;
            {var subQ0=sQuery(id+"F0.wireOp",EDGE,"E24.0");var subQ1=sQuery(id+"F0.wireOp",EDGE,"E16.0");var subQ2=makeQuery(id+"F0.imprint","INTERSECT",VERTEX,{"derivedFrom":[subQ1,subQ0]});Q1=makeQuery(id+"F0.imprint","IMPRINT",FACE,{"disambiguationData":[TD([[makeQuery(id+"F0.imprint","IMPRINT",EDGE,{"disambiguationData":[TD([[subQ2,-1.0]])],"derivedFrom":subQ1}),-1.0]])]});}
            var Q2;
            {var subQ0=sQuery(id+"F0.wireOp",EDGE,"E23.1");var subQ1=sQuery(id+"F0.wireOp",EDGE,"E20");var subQ2=makeQuery(id+"F0.imprint","INTERSECT",VERTEX,{"derivedFrom":[subQ1,subQ0]});Q2=makeQuery(id+"F0.imprint","IMPRINT",FACE,{"disambiguationData":[TD([[makeQuery(id+"F0.imprint","IMPRINT",EDGE,{"disambiguationData":[TD([[subQ2,1.0]])],"derivedFrom":subQ1}),-1.0]])]});}
            var Q3;
            {var subQ0=sQuery(id+"F0.wireOp",EDGE,"E23.2");var subQ1=sQuery(id+"F0.wireOp",EDGE,"E19");var subQ2=makeQuery(id+"F0.imprint","INTERSECT",VERTEX,{"derivedFrom":[subQ1,subQ0]});Q3=makeQuery(id+"F0.imprint","IMPRINT",FACE,{"disambiguationData":[TD([[makeQuery(id+"F0.imprint","IMPRINT",EDGE,{"disambiguationData":[TD([[subQ2,1.0]])],"derivedFrom":subQ1}),-1.0]])]});}
            var Q4;
            {var subQ0=sQuery(id+"F0.wireOp",EDGE,"E24.5");var subQ1=sQuery(id+"F0.wireOp",EDGE,"E17");var subQ2=makeQuery(id+"F0.imprint","INTERSECT",VERTEX,{"derivedFrom":[subQ1,subQ0]});Q4=makeQuery(id+"F0.imprint","IMPRINT",FACE,{"disambiguationData":[TD([[makeQuery(id+"F0.imprint","IMPRINT",EDGE,{"disambiguationData":[TD([[subQ2,-1.0]])],"derivedFrom":subQ1}),-1.0]])]});}
            var Q5;
            {var subQ0=sQuery(id+"F0.wireOp",EDGE,"E23.4");var subQ1=sQuery(id+"F0.wireOp",EDGE,"E18");var subQ2=makeQuery(id+"F0.imprint","INTERSECT",VERTEX,{"derivedFrom":[subQ1,subQ0]});Q5=makeQuery(id+"F0.imprint","IMPRINT",FACE,{"disambiguationData":[TD([[makeQuery(id+"F0.imprint","IMPRINT",EDGE,{"disambiguationData":[TD([[subQ2,1.0]])],"derivedFrom":subQ1}),-1.0]])]});}
            extrude(context, id + "F3", {"entities" : qUnion([Q0, Q1, Q2, Q3, Q4, Q5]), "operationType" : NewBodyOperationType.ADD, "depth" : 16 * mm});
        }
        {
            var Q0;
            Q0=makeQuery(id+"F0.imprint","IMPRINT",FACE,{"disambiguationData":[TD([[makeQuery(id+"F0.imprint","IMPRINT",EDGE,{"derivedFrom":sQuery(id+"F0.wireOp",EDGE,"E0")}),-1.0]])]});
            extrude(context, id + "F4", {"entities" : qUnion([Q0]), "operationType" : NewBodyOperationType.ADD, "depth" : 22 * mm});
        }
        {
            var Q0;
            Q0=makeQuery(id+"F0.imprint","IMPRINT",FACE,{"disambiguationData":[TD([[makeQuery(id+"F0.imprint","IMPRINT",EDGE,{"derivedFrom":sQuery(id+"F0.wireOp",EDGE,"E26")}),1.0]])]});
            var Q1;
            Q1=makeQuery(id+"F0.imprint","IMPRINT",FACE,{"disambiguationData":[TD([[makeQuery(id+"F0.imprint","IMPRINT",EDGE,{"derivedFrom":sQuery(id+"F0.wireOp",EDGE,"E29")}),1.0]])]});
            var Q2;
            Q2=makeQuery(id+"F0.imprint","IMPRINT",FACE,{"disambiguationData":[TD([[makeQuery(id+"F0.imprint","IMPRINT",EDGE,{"derivedFrom":sQuery(id+"F0.wireOp",EDGE,"E30")}),1.0]])]});
            var Q3;
            Q3=makeQuery(id+"F0.imprint","IMPRINT",FACE,{"disambiguationData":[TD([[makeQuery(id+"F0.imprint","IMPRINT",EDGE,{"derivedFrom":sQuery(id+"F0.wireOp",EDGE,"E31")}),1.0]])]});
            var Q4;
            Q4=makeQuery(id+"F0.imprint","IMPRINT",FACE,{"disambiguationData":[TD([[makeQuery(id+"F0.imprint","IMPRINT",EDGE,{"derivedFrom":sQuery(id+"F0.wireOp",EDGE,"E28")}),1.0]])]});
            var Q5;
            Q5=makeQuery(id+"F0.imprint","IMPRINT",FACE,{"disambiguationData":[TD([[makeQuery(id+"F0.imprint","IMPRINT",EDGE,{"derivedFrom":sQuery(id+"F0.wireOp",EDGE,"E27")}),1.0]])]});
            extrude(context, id + "F5", {"entities" : qUnion([Q0, Q1, Q2, Q3, Q4, Q5]), "operationType" : NewBodyOperationType.ADD, "depth" : 20 * mm});
        }
    });
